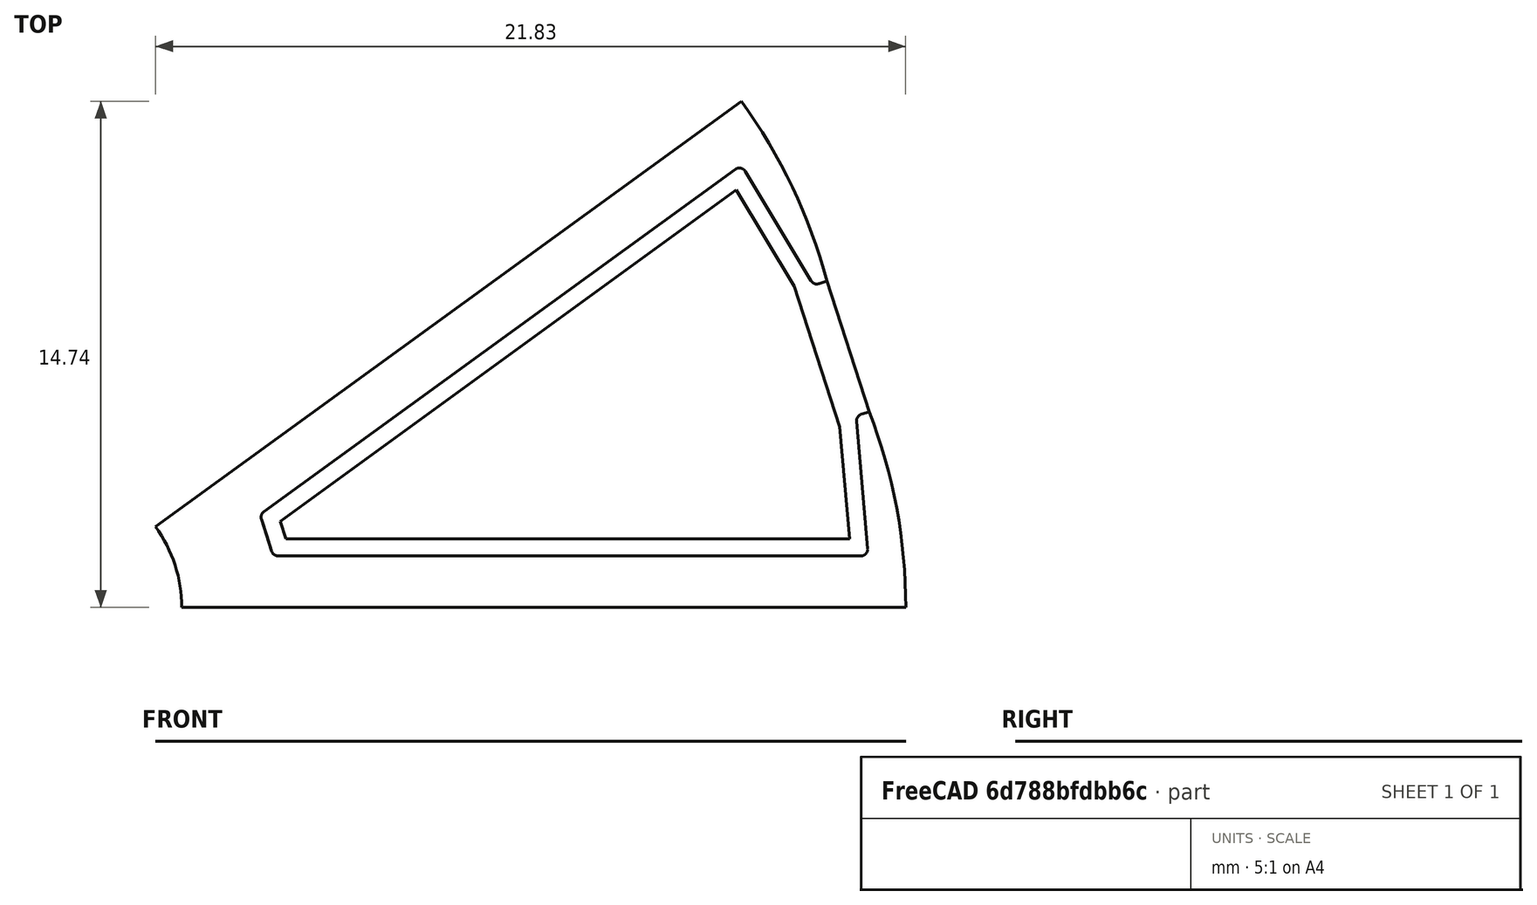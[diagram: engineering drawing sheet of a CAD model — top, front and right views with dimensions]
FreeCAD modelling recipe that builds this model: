
FCSTD DOCUMENT  (FreeCAD 0.18R4 (GitTag))
Label: winding3
License: All rights reserved
LicenseURL: http://en.wikipedia.org/wiki/All_rights_reserved
objects: Sketcher::SketchObject×7, Surface::Filling×3, PartDesign::Body×2, Spreadsheet::Sheet×1
note: 12 computed .brp shape members not serialized (recipe doc carries the construction recipe); baked Part::Feature solids carry a one-line shape summary decoded from their .brp

FEATURE [Spreadsheet::Sheet] Spreadsheet  label="Variables"
  cells = A2=slotNumber; B2(slotNumber)=10; A3=outerDiameter; B3(outerDiameter)=50.15; A4=innerDiameter; B4(innerDiameter)=8; A5=stackLength; B5(stackLength)=26; A6=stackingFactor; B6(stackingFactor)=0.95; A7=cuttingThickness; B7(cuttingThickness)=0.1; A8=skewAngle; B8(skewAngle)=0; A9=segmentAngle; B9(segmentAngle)==360 / slotNumber; A10=tipHeightReduction; B10(tipHeightReduction)=50; A11=toothThickness; B11(toothThickness)=3; A12=yokeThickness; B12(yokeThickness)=2.8; A13=tipHeight; B13(tipHeight)=0.8; A14=tipAngle; B14(tipAngle)=85; A15=openingLeft; B15(openingLeft)=2; A16=openingRight; B16(openingRight)=2; A17=slotIsolation; B17(slotIsolation)=0.5; A18=windingAngle; B18(windingAngle)=35; A19=heightRatio; B19(heightRatio)=40; A20=roundingRadii; B20(roundingRadii)=0.2; A21=coilAxialHeight; B21(coilAxialHeight)=15
FEATURE [Sketcher::SketchObject] Sketch003  label="StatorSketch"
  MapMode = 5
  Support = -> [XY_Plane]
  expr: Constraints[71] = Variables.innerDiameter / 2
  expr: Constraints[26] = Variables.toothThickness / 2
  expr: Constraints[9] = Variables.segmentAngle
  expr: Constraints[27] = Variables.innerDiameter / 2 + Variables.yokeThickness
  expr: Constraints[35] = Variables.roundingRadii
  expr: Constraints[61] = Variables.tipHeight
  expr: Constraints[23] = Variables.tipAngle
  expr: Constraints[16] = Variables.tipHeight * (1 - Variables.tipHeightReduction / 100)
  expr: Constraints[12] = Variables.openingLeft
  expr: Constraints[72] = Variables.segmentAngle / 2
  expr: Constraints[5] = Variables.outerDiameter
  sketch-geometry (29):
    g0: ArcOfCircle [constr] CenterX=0 CenterY=0 CenterZ=0 NormalX=0 NormalY=0 NormalZ=1 AngleXU=0 Radius=25.075 StartAngle=0 EndAngle=0.628319
    g1: LineSegment [constr] StartX=0 StartY=0 StartZ=0 EndX=20.2861 EndY=14.7387 EndZ=0
    g2: LineSegment [constr] StartX=0 StartY=0 StartZ=0 EndX=25.075 EndY=-1.5e-15 EndZ=0
    g3: LineSegment [constr] StartX=0 StartY=0 StartZ=0 EndX=23.8477 EndY=7.7486 EndZ=0
    g4: LineSegment [constr] StartX=16.3086 StartY=19.0469 StartZ=0 EndX=23.1543 EndY=9.62455 EndZ=0
    g5: LineSegment [constr] StartX=23.1543 StartY=9.62455 StartZ=0 EndX=22.5448 EndY=9.4265 EndZ=0
    g6: LineSegment [constr] StartX=22.3935 StartY=9.37734 StartZ=0 EndX=22.7739 EndY=9.50095 EndZ=0
    g7: ArcOfCircle CenterX=7.52715 CenterY=5.4688 CenterZ=0 NormalX=0 NormalY=0 NormalZ=1 AngleXU=0 Radius=15.7709 StartAngle=0.25854 EndAngle=0.628319
    g8: LineSegment StartX=22.3116 StartY=9.5137 StartZ=0 EndX=20.3985 EndY=12.6975 EndZ=0
    g9: LineSegment StartX=20.1095 StartY=12.7563 StartZ=0 EndX=6.38936 EndY=2.78804 EndZ=0
    g10: LineSegment StartX=6.31671 StartY=2.56443 StartZ=0 EndX=6.46718 EndY=2.10132 EndZ=0
    g11: LineSegment [constr] StartX=6.38936 StartY=2.78804 StartZ=0 EndX=5.50768 EndY=4.00157 EndZ=0
    g12: LineSegment StartX=6.46718 StartY=2.10132 StartZ=0 EndX=6.61766 EndY=1.6382 EndZ=0
    g13: LineSegment StartX=6.80787 StartY=1.5 StartZ=0 EndX=23.7669 EndY=1.5 EndZ=0
    g14: LineSegment StartX=23.9662 StartY=1.71743 StartZ=0 EndX=23.6424 EndY=5.41766 EndZ=0
    g15: LineSegment StartX=23.7799 StartY=5.6253 StartZ=0 EndX=24.009 EndY=5.69975 EndZ=0
    g16: ArcOfCircle CenterX=9.30407 CenterY=3.287e-13 CenterZ=0 NormalX=0 NormalY=0 NormalZ=1 AngleXU=0 Radius=15.7709 StartAngle=0 EndAngle=0.369778
    g17: ArcOfCircle CenterX=23.8417 CenterY=5.43509 CenterZ=0 NormalX=0 NormalY=0 NormalZ=1 AngleXU=0 Radius=0.2 StartAngle=1.88496 EndAngle=3.22886
    g18: ArcOfCircle CenterX=23.7669 CenterY=1.7 CenterZ=0 NormalX=0 NormalY=0 NormalZ=1 AngleXU=0 Radius=0.2 StartAngle=4.71239 EndAngle=6.37045
    g19: ArcOfCircle CenterX=6.80787 CenterY=1.7 CenterZ=0 NormalX=0 NormalY=0 NormalZ=1 AngleXU=0 Radius=0.2 StartAngle=3.45575 EndAngle=4.71239
    g20: ArcOfCircle CenterX=20.2271 CenterY=12.5945 CenterZ=0 NormalX=0 NormalY=0 NormalZ=1 AngleXU=0 Radius=0.2 StartAngle=0.541052 EndAngle=2.19911
    g21: ArcOfCircle CenterX=22.483 CenterY=9.61671 CenterZ=0 NormalX=0 NormalY=0 NormalZ=1 AngleXU=0 Radius=0.2 StartAngle=3.68264 EndAngle=5.02655
    g22: ArcOfCircle CenterX=6.50692 CenterY=2.62624 CenterZ=0 NormalX=0 NormalY=0 NormalZ=1 AngleXU=0 Radius=0.2 StartAngle=2.19911 EndAngle=3.45575
    g23: LineSegment [constr] StartX=22.3116 StartY=9.5137 StartZ=0 EndX=22.3935 EndY=9.37734 EndZ=0
    g24: LineSegment [constr] StartX=22.3935 StartY=9.37734 StartZ=0 EndX=22.5448 EndY=9.4265 EndZ=0
    g25: LineSegment StartX=22.5448 StartY=9.4265 StartZ=0 EndX=22.7739 EndY=9.50095 EndZ=0
    g26: LineSegment StartX=20.2861 StartY=14.7387 StartZ=0 EndX=3.23607 EndY=2.35114 EndZ=0
    g27: LineSegment StartX=4 StartY=-2e-16 StartZ=0 EndX=25.075 EndY=-1.5e-15 EndZ=0
    g28: ArcOfCircle CenterX=0 CenterY=0 CenterZ=0 NormalX=0 NormalY=0 NormalZ=1 AngleXU=0 Radius=4 StartAngle=0 EndAngle=0.628319
  constraints (73):
    c: Coincident(g0,g-1)
    c: Coincident(g1,g0)
    c: Coincident(g1,g0)
    c: Coincident(g2,g0)
    c: Coincident(g2,g0)
    c: Diameter(g0) = 50.15
    c: Coincident(g3,g0)
    c: PointOnObject(g3,g0)
    c: Symmetric(g0,g0,g3)
    c: Angle(g2,g1) = 0.628319
    c: PointOnObject(g4,g0)
    c: Symmetric(g4,g4,g1)
    c: Distance(g4,g3) = 2
    c: Coincident(g5,g4)
    c: Parallel(g5,g3)
    c: PointOnObject(g6,g5)
    c: Distance(g6) = 0.4
    c: Coincident(g7,g0)
    c: Coincident(g7,g6)
    c: PointOnObject(g7,g1)
    c: PointOnObject(g10,g3)
    c: Perpendicular(g3,g10)
    c: Parallel(g1,g9)
    c: Angle(g9,g8) = 1.48353
    c: PointOnObject(g11,g1)
    c: Perpendicular(g1,g11)
    c: Distance(g11) = 1.5
    c: Distance(g-1,g10) = 6.8
    c: Coincident(g12,g10)
    c: Symmetric(g15,g7,g3)
    c: PointOnObject(g16,g2)
    c: Coincident(g16,g0)
    c: Coincident(g16,g15)
    c: Tangent(g14,g17) = 1.5708
    c: Tangent(g15,g17) = 1.5708
    c: Radius(g17) = 0.2
    c: Tangent(g13,g18) = -1.5708
    c: Tangent(g14,g18) = -1.5708
    c: Tangent(g12,g19) = -1.5708
    c: Tangent(g13,g19) = -1.5708
    c: Tangent(g8,g20) = -1.5708
    c: Tangent(g9,g20) = -1.5708
    c: Tangent(g5,g21) = 1.5708
    c: Tangent(g8,g21) = 1.5708
    c: Tangent(g10,g22) = -1.5708
    c: Tangent(g9,g22) = -1.5708
    c: Coincident(g11,g9)
    c: Equal(g17,g18)
    c: Equal(g19,g17)
    c: Equal(g22,g17)
    c: Equal(g20,g17)
    c: Symmetric(g13,g9,g3)
    c: Symmetric(g14,g8,g3)
    c: Symmetric(g14,g8,g3)
    c: Equal(g21,g17)
    c: Coincident(g23,g8)
    c: Coincident(g24,g23)
    c: Coincident(g24,g5)
    c: Parallel(g23,g8)
    c: Parallel(g24,g5)
    c: Coincident(g6,g23)
    c: Distance(g6,g4) = 0.8
    c: Coincident(g25,g21)
    c: Coincident(g25,g7)
    c: Coincident(g26,g7)
    c: PointOnObject(g26,g1)
    c: PointOnObject(g27,g2)
    c: Coincident(g27,g16)
    c: Coincident(g28,g-1)
    c: Coincident(g28,g26)
    c: Coincident(g28,g27)
    c: Radius(g28) = 4
    c: Angle(g-1,g3) = 0.314159
FEATURE [Sketcher::SketchObject] Sketch  label="StatorSde"
  MapMode = 5
  Support = -> [XY_Plane001]
  expr: Constraints[20] = Variables.stackLength
  expr: Constraints[17] = Variables.innerDiameter
  expr: Constraints[16] = Variables.outerDiameter
  sketch-geometry (8):
    g0: LineSegment StartX=-13 StartY=25.075 StartZ=0 EndX=13 EndY=25.075 EndZ=0
    g1: LineSegment StartX=13 StartY=25.075 StartZ=0 EndX=13 EndY=4 EndZ=0
    g2: LineSegment StartX=13 StartY=4 StartZ=0 EndX=-13 EndY=4 EndZ=0
    g3: LineSegment StartX=-13 StartY=4 StartZ=0 EndX=-13 EndY=25.075 EndZ=0
    g4: LineSegment StartX=-13 StartY=-4 StartZ=0 EndX=13 EndY=-4 EndZ=0
    g5: LineSegment StartX=13 StartY=-4 StartZ=0 EndX=13 EndY=-25.075 EndZ=0
    g6: LineSegment StartX=13 StartY=-25.075 StartZ=0 EndX=-13 EndY=-25.075 EndZ=0
    g7: LineSegment StartX=-13 StartY=-25.075 StartZ=0 EndX=-13 EndY=-4 EndZ=0
  constraints (21):
    c: Coincident(g0,g1)
    c: Coincident(g1,g2)
    c: Coincident(g2,g3)
    c: Coincident(g3,g0)
    c: Horizontal(g0)
    c: Vertical(g1)
    c: Vertical(g3)
    c: Coincident(g4,g5)
    c: Coincident(g5,g6)
    c: Coincident(g6,g7)
    c: Coincident(g7,g4)
    c: Horizontal(g6)
    c: Vertical(g5)
    c: Vertical(g7)
    c: Symmetric(g2,g1,g-2)
    c: Symmetric(g4,g4,g-2)
    c: DistanceY(g6,g0) = 50.15
    c: DistanceY(g4,g2) = 8
    c: Symmetric(g4,g2,g-1)
    c: Equal(g7,g3)
    c: DistanceX(g6,g6) = 26
FEATURE [Sketcher::SketchObject] Sketch009  label="WindingSide"
  ExternalGeometry = -> [Sketch]
  MapMode = 5
  Support = -> [XY_Plane001]
  expr: Constraints[18] = Variables.coilAxialHeight
  expr: Constraints[8] = Variables.coilAxialHeight
  sketch-geometry (12):
    g0: ArcOfEllipse CenterX=-13 CenterY=0 CenterZ=0 NormalX=0 NormalY=0 NormalZ=1 MajorRadius=25.075 MinorRadius=15 AngleXU=1.5708 StartAngle=1e-16 EndAngle=3.14159
    g1: LineSegment [constr] StartX=-13 StartY=25.075 StartZ=0 EndX=-13 EndY=-25.075 EndZ=0
    g2: LineSegment [constr] StartX=-28 StartY=0 StartZ=0 EndX=2 EndY=0 EndZ=0
    g3: GeomPoint X=-13 Y=20.0937 Z=0
    g4: GeomPoint X=-13 Y=-20.0937 Z=0
    g5: LineSegment StartX=-13 StartY=25.075 StartZ=0 EndX=-13 EndY=-25.075 EndZ=0
    g6: ArcOfEllipse CenterX=13 CenterY=0 CenterZ=0 NormalX=0 NormalY=0 NormalZ=1 MajorRadius=25.075 MinorRadius=15 AngleXU=-1.5708 StartAngle=-9.8e-15 EndAngle=3.14159
    g7: LineSegment [constr] StartX=13 StartY=-25.075 StartZ=0 EndX=13 EndY=25.075 EndZ=0
    g8: LineSegment [constr] StartX=28 StartY=0 StartZ=0 EndX=-2 EndY=0 EndZ=0
    g9: GeomPoint X=13 Y=-20.0937 Z=0
    g10: GeomPoint X=13 Y=20.0937 Z=0
    g11: LineSegment StartX=13 StartY=25.075 StartZ=0 EndX=13 EndY=-25.075 EndZ=0
  constraints (18):
    c: InternalAlignment(g1-g4 -> g0) x4
    c: PointOnObject(g0,g-4)
    c: Horizontal(g2)
    c: PointOnObject(g0,g-1)
    c: PointOnObject(g1,g-3)
    c: DistanceX(g2,g0) = 15
    c: Coincident(g0,g-3)
    c: Coincident(g5,g0)
    c: Coincident(g5,g0)
    c: InternalAlignment(g7-g10 -> g6) x4
    c: PointOnObject(g6,g-1)
    c: Coincident(g6,g-6)
    c: DistanceX(g6,g8) = 15
    c: Coincident(g6,g7)
    c: Horizontal(g8)
    c: PointOnObject(g6,g7)
    c: Coincident(g11,g6)
    c: Coincident(g11,g6)
FEATURE [PartDesign::Body] Body001  label="SideView"
  Group = -> [Sketch,Sketch009]
  Origin = -> Origin001
FEATURE [Sketcher::SketchObject] Sketch011  label="TerminalSketch"
  ExternalGeometry = -> [Sketch003]
  MapMode = 5
  Support = -> [XY_Plane]
  expr: Constraints[17] = Variables.innerDiameter / 2 + Variables.yokeThickness + Variables.slotIsolation
  expr: Constraints[31] = Variables.slotIsolation
  expr: Constraints[28] = 90
  expr: Constraints[18] = Variables.toothThickness / 2 + Variables.slotIsolation
  expr: Constraints[2] = (Variables.outerDiameter / 2 - Variables.innerDiameter / 2 - Variables.yokeThickness - Variables.tipHeight) * Variables.heightRatio / 100
  sketch-geometry (12):
    g0: LineSegment [constr] StartX=6.46718 StartY=2.10132 StartZ=0 EndX=13.1151 EndY=4.26134 EndZ=0
    g1: LineSegment StartX=21.8217 StartY=9.35453 StartZ=0 EndX=20.137 EndY=12.1583 EndZ=0
    g2: LineSegment StartX=20.137 StartY=12.1583 StartZ=0 EndX=6.85959 EndY=2.51165 EndZ=0
    g3: LineSegment StartX=6.85959 StartY=2.51165 StartZ=0 EndX=7.02583 EndY=2 EndZ=0
    g4: LineSegment StartX=7.02583 StartY=2 StartZ=0 EndX=23.4376 EndY=2 EndZ=0
    g5: LineSegment StartX=23.4376 StartY=2 StartZ=0 EndX=23.1525 EndY=5.25848 EndZ=0
    g6: LineSegment StartX=23.1525 StartY=5.25848 StartZ=0 EndX=21.8217 EndY=9.35453 EndZ=0
    g7: GeomPoint X=6.94271 Y=2.25582 Z=0
    g8: LineSegment [constr] StartX=23.6424 StartY=5.41766 StartZ=0 EndX=22.3116 EndY=9.5137 EndZ=0
    g9: LineSegment [constr] StartX=20.137 StartY=12.1583 StartZ=0 EndX=19.8785 EndY=12.5885 EndZ=0
    g10: LineSegment [constr] StartX=20.137 StartY=12.1583 StartZ=0 EndX=20.5672 EndY=12.4168 EndZ=0
    g11: LineSegment [constr] StartX=12.8773 StartY=4.18409 StartZ=0 EndX=13.3528 EndY=4.3386 EndZ=0
  constraints (32):
    c: Coincident(g0,g-6)
    c: Perpendicular(g0,g-5)
    c: Distance(g0) = 6.99
    c: Coincident(g1,g2)
    c: Coincident(g2,g3)
    c: Coincident(g3,g4)
    c: Horizontal(g4)
    c: Coincident(g4,g5)
    c: Coincident(g5,g6)
    c: Coincident(g6,g1)
    c: Parallel(g1,g-3)
    c: Parallel(g5,g-8)
    c: Parallel(g6,g3)
    c: Symmetric(g3,g2,g0)
    c: Symmetric(g4,g1,g0)
    c: PointOnObject(g7,g3)
    c: PointOnObject(g7,g0)
    c: Distance(g-1,g7) = 7.3
    c: DistanceY(g-1,g3) = 2
    c: Coincident(g8,g-8)
    c: Coincident(g8,g-3)
    c: Equal(g8,g6)
    c: Coincident(g9,g1)
    c: PointOnObject(g9,g-4)
    c: Coincident(g10,g1)
    c: PointOnObject(g10,g-3)
    c: Angle(g10,g9) = 1.5708
    c: Equal(g9,g10)
    c: Angle(g1,g10) = 1.5708
    c: PointOnObject(g11,g0)
    c: Symmetric(g11,g11,g0)
    c: Distance(g11,g11) = 0.5
FEATURE [Sketcher::SketchObject] Sketch012  label="SlotSketch"
  ExternalGeometry = -> [Sketch003]
  MapMode = 5
  Support = -> [XY_Plane]
  sketch-geometry (14):
    g0: LineSegment StartX=22.7739 StartY=9.50095 StartZ=0 EndX=22.5448 EndY=9.4265 EndZ=0
    g1: LineSegment StartX=22.3116 StartY=9.5137 StartZ=0 EndX=20.3985 EndY=12.6975 EndZ=0
    g2: LineSegment StartX=20.1095 StartY=12.7563 StartZ=0 EndX=6.38936 EndY=2.78804 EndZ=0
    g3: LineSegment StartX=6.31671 StartY=2.56443 StartZ=0 EndX=6.61766 EndY=1.6382 EndZ=0
    g4: LineSegment StartX=6.80787 StartY=1.5 StartZ=0 EndX=23.7669 EndY=1.5 EndZ=0
    g5: LineSegment StartX=23.9662 StartY=1.71743 StartZ=0 EndX=23.6424 EndY=5.41766 EndZ=0
    g6: LineSegment StartX=23.7799 StartY=5.6253 StartZ=0 EndX=24.009 EndY=5.69975 EndZ=0
    g7: ArcOfCircle CenterX=22.483 CenterY=9.61671 CenterZ=0 NormalX=0 NormalY=0 NormalZ=1 AngleXU=0 Radius=0.2 StartAngle=3.68264 EndAngle=5.02655
    g8: ArcOfCircle CenterX=20.2271 CenterY=12.5945 CenterZ=0 NormalX=0 NormalY=0 NormalZ=1 AngleXU=0 Radius=0.2 StartAngle=0.541052 EndAngle=2.19911
    g9: ArcOfCircle CenterX=6.50692 CenterY=2.62624 CenterZ=0 NormalX=0 NormalY=0 NormalZ=1 AngleXU=0 Radius=0.2 StartAngle=2.19911 EndAngle=3.45575
    g10: ArcOfCircle CenterX=6.80787 CenterY=1.7 CenterZ=0 NormalX=0 NormalY=0 NormalZ=1 AngleXU=0 Radius=0.2 StartAngle=3.45575 EndAngle=4.71239
    g11: ArcOfCircle CenterX=23.7669 CenterY=1.7 CenterZ=0 NormalX=0 NormalY=0 NormalZ=1 AngleXU=0 Radius=0.2 StartAngle=4.71239 EndAngle=6.37045
    g12: ArcOfCircle CenterX=23.8417 CenterY=5.43509 CenterZ=0 NormalX=0 NormalY=0 NormalZ=1 AngleXU=0 Radius=0.2 StartAngle=1.88496 EndAngle=3.22886
    g13: LineSegment StartX=24.009 StartY=5.69975 StartZ=0 EndX=22.7739 EndY=9.50095 EndZ=0
  constraints (34):
    c: Coincident(g0,g-3)
    c: Coincident(g0,g-4)
    c: Coincident(g1,g-5)
    c: Coincident(g1,g-6)
    c: Coincident(g2,g-7)
    c: Coincident(g2,g-8)
    c: Coincident(g3,g-9)
    c: Coincident(g3,g-11)
    c: Coincident(g4,g-13)
    c: Coincident(g4,g-12)
    c: Coincident(g5,g-14)
    c: Coincident(g5,g-15)
    c: Coincident(g6,g-16)
    c: Coincident(g6,g-16)
    c: Coincident(g7,g-4)
    c: Coincident(g7,g0)
    c: Coincident(g7,g1)
    c: Coincident(g8,g-6)
    c: Coincident(g8,g2)
    c: Coincident(g8,g1)
    c: Coincident(g9,g3)
    c: Coincident(g9,g2)
    c: Tangent(g9,g-8)
    c: Coincident(g10,g3)
    c: Coincident(g10,g4)
    c: Tangent(g10,g-11)
    c: Coincident(g11,g4)
    c: Coincident(g11,g5)
    c: Tangent(g11,g-13)
    c: Coincident(g12,g5)
    c: Tangent(g12,g-15)
    c: Coincident(g12,g6)
    c: Coincident(g13,g6)
    c: Coincident(g13,g0)
FEATURE [Sketcher::SketchObject] Sketch013  label="YokeLine"
  ExternalGeometry = -> [Sketch003]
  MapMode = 5
  Support = -> [XY_Plane]
  sketch-geometry (1):
    g0: LineSegment StartX=6.46718 StartY=2.10132 StartZ=0 EndX=3.80423 EndY=1.23607 EndZ=0
  constraints (3):
    c: Coincident(g0,g-4)
    c: PointOnObject(g0,g-3)
    c: Angle(g-4,g0) = 1.5708
FEATURE [Sketcher::SketchObject] Sketch014  label="ToothLine"
  ExternalGeometry = -> [Sketch003]
  MapMode = 5
  Support = -> [XY_Plane]
  expr: Constraints[2] = Variables.toothThickness
  sketch-geometry (1):
    g0: LineSegment StartX=13.2494 StartY=7.77219 StartZ=0 EndX=11.4861 EndY=10.1992 EndZ=0
  constraints (3):
    c: Symmetric(g-3,g-3,g0)
    c: Angle(g-3,g0) = 1.5708
    c: Distance(g0) = 3
FEATURE [PartDesign::Body] Body  label="TopView"
  Group = -> [Sketch003,Sketch011,Sketch012,Sketch013,Sketch014]
  Origin = -> Origin
FEATURE [Surface::Filling] Surface  label="StatorSketch_Surface"
  Anisotropy = false
  BoundaryEdges = -> [Sketch003]
  BoundaryOrder = [0,0,0,0,0,0,0,0,0,0,0,0,0,0,0,0,0,0,0]
  Degree = 3
  Iterations = 2
  MaximumDegree = 8
  MaximumSegments = 9
  PointsOnCurve = 15
  TolAngular = 0.01
  TolCurvature = 0.1
  Tolerance2d = 1e-05
  Tolerance3d = 0.0001
FEATURE [Surface::Filling] Surface001  label="TerminalSketch_Surface"
  Anisotropy = false
  BoundaryEdges = -> [Sketch011]
  BoundaryOrder = [0,0,0,0,0,0]
  Degree = 3
  Iterations = 2
  MaximumDegree = 8
  MaximumSegments = 9
  PointsOnCurve = 15
  TolAngular = 0.01
  TolCurvature = 0.1
  Tolerance2d = 1e-05
  Tolerance3d = 0.0001
FEATURE [Surface::Filling] Surface002  label="SlotSketch_Surface"
  Anisotropy = false
  BoundaryEdges = -> [Sketch012]
  BoundaryOrder = [0,0,0,0,0,0,0,0,0,0,0,0,0,0]
  Degree = 3
  Iterations = 2
  MaximumDegree = 8
  MaximumSegments = 9
  PointsOnCurve = 15
  TolAngular = 0.01
  TolCurvature = 0.1
  Tolerance2d = 1e-05
  Tolerance3d = 0.0001
